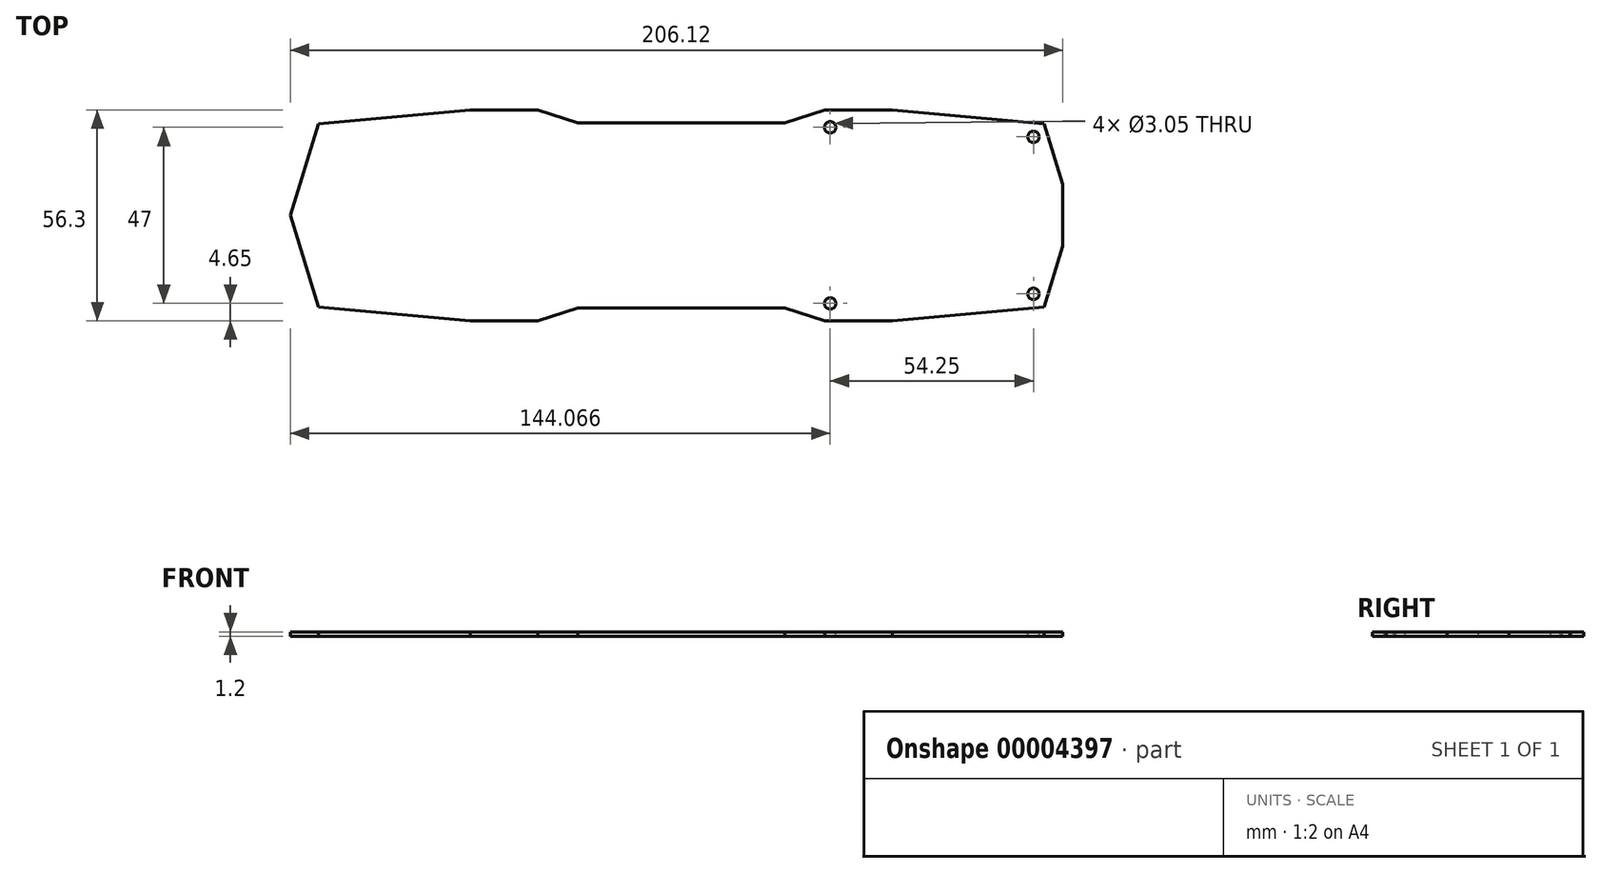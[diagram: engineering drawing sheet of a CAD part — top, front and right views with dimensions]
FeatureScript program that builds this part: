
annotation { "Feature Type Name" : "Feature", "Feature Type Description" : "" }
export const myFeature = defineFeature(function(context is Context, id is Id, definition is map)
    precondition{}
    {
        {
            var Q0;
            Q0=qCreatedBy(makeId("Top.planeOp"),FACE);
            var sketch = newSketch(context, id + "F0", { "sketchPlane" : qUnion([Q0])});
            skLineSegment(sketch, "E0", {"start": v(0, 0) * mm, "end": v(-206.12, 0) * mm, "construction": true});
            skLineSegment(sketch, "E1", {"start": v(0, 0) * mm, "end": v(0, 8.25) * mm});
            skLineSegment(sketch, "E2", {"start": v(0, 8.25) * mm, "end": v(-4.97, 24.5) * mm});
            skLineSegment(sketch, "E3", {"start": v(-4.97, 24.5) * mm, "end": v(-45.5, 28.15) * mm});
            skLineSegment(sketch, "E4.trimOffspring", {"start": v(-45.5, 28.15) * mm, "end": v(-63.5, 28.15) * mm});
            skLineSegment(sketch, "E5.0", {"start": v(-101.8, 0) * mm, "end": v(-101.8, 28.15) * mm, "construction": true});
            skPoint(sketch, "E6.orphan", {"position": v(0, -28.15) * mm});
            skPoint(sketch, "E7.orphan", {"position": v(-205, -28.15) * mm});
            skPoint(sketch, "E8.start.orphan", {"position": v(-205, 28.15) * mm});
            skLineSegment(sketch, "E9.0.MirrorCS", {"start": v(-206.12, 0) * mm, "end": v(-198.63, 24.5) * mm});
            skLineSegment(sketch, "E9.1.MirrorCS", {"start": v(-158.1, 28.15) * mm, "end": v(-140.1, 28.15) * mm});
            skLineSegment(sketch, "E9.3.MirrorCS", {"start": v(-198.63, 24.5) * mm, "end": v(-158.1, 28.15) * mm});
            skPoint(sketch, "E10.orphan", {"position": v(-205, 0) * mm});
            skLineSegment(sketch, "E11.1.MirrorCS", {"start": v(-203.6, 8.25) * mm, "end": v(-198.63, 24.5) * mm});
            skPoint(sketch, "E11.5.MirrorP", {"position": v(1.4, 28.15) * mm});
            skLineSegment(sketch, "E12.0.MirrorCS", {"start": v(-203.6, -8.25) * mm, "end": v(-198.63, -24.5) * mm});
            skLineSegment(sketch, "E12.1.MirrorCS", {"start": v(-158.1, -28.15) * mm, "end": v(-140.1, -28.15) * mm});
            skLineSegment(sketch, "E12.2.MirrorCS", {"start": v(-4.97, -24.5) * mm, "end": v(-45.5, -28.15) * mm});
            skLineSegment(sketch, "E12.3.MirrorCS", {"start": v(-198.63, -24.5) * mm, "end": v(-158.1, -28.15) * mm});
            skLineSegment(sketch, "E12.4.MirrorCS", {"start": v(-45.5, -28.15) * mm, "end": v(-63.5, -28.15) * mm});
            skLineSegment(sketch, "E12.5.MirrorCS", {"start": v(0, -8.25) * mm, "end": v(-4.97, -24.5) * mm});
            skPoint(sketch, "E12.6.MirrorP", {"position": v(1.4, -28.15) * mm});
            skLineSegment(sketch, "E12.7.MirrorCS", {"start": v(-198.63, -24.5) * mm, "end": v(-158.1, -28.15) * mm});
            skLineSegment(sketch, "E12.8.MirrorCS", {"start": v(-206.12, 0) * mm, "end": v(-198.63, -24.5) * mm});
            skLineSegment(sketch, "E12.11.MirrorCS", {"start": v(-45.5, -28.15) * mm, "end": v(-63.5, -28.15) * mm});
            skLineSegment(sketch, "E12.12.MirrorCS", {"start": v(0, 0) * mm, "end": v(0, -8.25) * mm});
            skLineSegment(sketch, "E12.13.MirrorCS", {"start": v(0, -8.25) * mm, "end": v(-4.97, -24.5) * mm});
            skLineSegment(sketch, "E12.14.MirrorCS", {"start": v(-4.97, -24.5) * mm, "end": v(-45.5, -28.15) * mm});
            skLineSegment(sketch, "E12.15.MirrorCS", {"start": v(-101.8, 0) * mm, "end": v(-101.8, -28.15) * mm, "construction": true});
            skLineSegment(sketch, "E12.16.MirrorCS", {"start": v(-158.1, -28.15) * mm, "end": v(-140.1, -28.15) * mm});
            skPoint(sketch, "E13.orphan", {"position": v(2.52, 0) * mm});
            skPoint(sketch, "E11.0.MirrorCS.start.orphan", {"position": v(-203.6, 0) * mm});
            skLineSegment(sketch, "E14", {"start": v(-74.2, 24.75) * mm, "end": v(-63.5, 28.15) * mm});
            skLineSegment(sketch, "E15", {"start": v(-74.2, -24.75) * mm, "end": v(-63.5, -28.15) * mm});
            skLineSegment(sketch, "E16.0.MirrorCS", {"start": v(-129.4, 24.75) * mm, "end": v(-140.1, 28.15) * mm});
            skLineSegment(sketch, "E17.0.MirrorCS", {"start": v(-129.4, -24.75) * mm, "end": v(-140.1, -28.15) * mm});
            skLineSegment(sketch, "E18.trimOffspring", {"start": v(-74.2, -24.75) * mm, "end": v(-129.4, -24.75) * mm});
            skLineSegment(sketch, "E19.trimOffspring", {"start": v(-74.2, 24.75) * mm, "end": v(-129.4, 24.75) * mm});
            skSolve(sketch);
        }
        {
            var Q0;
            Q0=qSketchRegion(id+"F0",true);
            extrude(context, id + "F1", {"entities" : qUnion([Q0]), "depth" : 1.2 * mm});
        }
        {
            var Q0;
            Q0=makeQuery(id+"F1.opExtrude","CAP_FACE",FACE,{"disambiguationData":[OSD([sQuery(id+"F0.wireOp",EDGE,"E11.1.MirrorCS"),sQuery(id+"F0.wireOp",EDGE,"E2"),sQuery(id+"F0.wireOp",EDGE,"E4.trimOffspring"),sQuery(id+"F0.wireOp",EDGE,"E3"),sQuery(id+"F0.wireOp",EDGE,"E9.3.MirrorCS"),sQuery(id+"F0.wireOp",EDGE,"E9.1.MirrorCS"),sQuery(id+"F0.wireOp",EDGE,"E12.7.MirrorCS"),sQuery(id+"F0.wireOp",EDGE,"E12.8.MirrorCS"),sQuery(id+"F0.wireOp",EDGE,"E12.11.MirrorCS"),sQuery(id+"F0.wireOp",EDGE,"E12.12.MirrorCS"),sQuery(id+"F0.wireOp",EDGE,"E12.13.MirrorCS"),sQuery(id+"F0.wireOp",EDGE,"E12.14.MirrorCS"),sQuery(id+"F0.wireOp",EDGE,"E12.16.MirrorCS"),sQuery(id+"F0.wireOp",EDGE,"E14"),sQuery(id+"F0.wireOp",EDGE,"E15"),sQuery(id+"F0.wireOp",EDGE,"E16.0.MirrorCS"),sQuery(id+"F0.wireOp",EDGE,"E17.0.MirrorCS"),sQuery(id+"F0.wireOp",EDGE,"E18.trimOffspring"),sQuery(id+"F0.wireOp",EDGE,"E19.trimOffspring")])],"isStart":false});
            var sketch = newSketch(context, id + "F2", { "sketchPlane" : qUnion([Q0])});
            skLineSegment(sketch, "E20.0", {"start": v(-3.59, 7.15) * mm, "end": v(-8.55, 23.4) * mm, "construction": true});
            skLineSegment(sketch, "E21.0", {"start": v(-3.59, -7.15) * mm, "end": v(-8.55, -23.4) * mm, "construction": true});
            skLineSegment(sketch, "E22", {"start": v(0, 0) * mm, "end": v(-60.09, 0) * mm, "construction": true});
            skLineSegment(sketch, "E23.0", {"start": v(0, 20.95) * mm, "end": v(-60.09, 20.95) * mm, "construction": true});
            skLineSegment(sketch, "E24.0", {"start": v(0, -20.95) * mm, "end": v(-60.09, -20.95) * mm, "construction": true});
            skCircle(sketch, "E25", {"center": v(-7.8, 20.95) * mm, "radius": 1.52 * mm});
            skCircle(sketch, "E26", {"center": v(-7.8, -20.95) * mm, "radius": 1.52 * mm});
            skSolve(sketch);
        }
        {
            var Q0;
            {Q0=qUnion([makeQuery(id+"F2.imprint","IMPRINT",FACE,{"disambiguationData":[TD([[makeQuery(id+"F2.imprint","IMPRINT",EDGE,{"derivedFrom":sQuery(id+"F2.wireOp",EDGE,"E25")}),1.0]])]}),makeQuery(id+"F2.imprint","IMPRINT",FACE,{"disambiguationData":[TD([[makeQuery(id+"F2.imprint","IMPRINT",EDGE,{"derivedFrom":sQuery(id+"F2.wireOp",EDGE,"E26")}),1.0]])]})]);}
            extrude(context, id + "F3", {"entities" : qUnion([Q0]), "operationType" : NewBodyOperationType.REMOVE, "endBound" : BoundingType.THROUGH_ALL, "oppositeDirection" : true, "depth" : 25 * mm});
        }
        {
            var Q0;
            Q0=makeQuery(id+"F1.opExtrude","CAP_FACE",FACE,{"disambiguationData":[OSD([sQuery(id+"F0.wireOp",EDGE,"E11.1.MirrorCS"),sQuery(id+"F0.wireOp",EDGE,"E2"),sQuery(id+"F0.wireOp",EDGE,"E4.trimOffspring"),sQuery(id+"F0.wireOp",EDGE,"E3"),sQuery(id+"F0.wireOp",EDGE,"E9.3.MirrorCS"),sQuery(id+"F0.wireOp",EDGE,"E9.1.MirrorCS"),sQuery(id+"F0.wireOp",EDGE,"E12.7.MirrorCS"),sQuery(id+"F0.wireOp",EDGE,"E12.8.MirrorCS"),sQuery(id+"F0.wireOp",EDGE,"E12.11.MirrorCS"),sQuery(id+"F0.wireOp",EDGE,"E12.12.MirrorCS"),sQuery(id+"F0.wireOp",EDGE,"E12.13.MirrorCS"),sQuery(id+"F0.wireOp",EDGE,"E12.14.MirrorCS"),sQuery(id+"F0.wireOp",EDGE,"E12.16.MirrorCS"),sQuery(id+"F0.wireOp",EDGE,"E14"),sQuery(id+"F0.wireOp",EDGE,"E15"),sQuery(id+"F0.wireOp",EDGE,"E16.0.MirrorCS"),sQuery(id+"F0.wireOp",EDGE,"E17.0.MirrorCS"),sQuery(id+"F0.wireOp",EDGE,"E18.trimOffspring"),sQuery(id+"F0.wireOp",EDGE,"E19.trimOffspring")])],"isStart":false});
            var sketch = newSketch(context, id + "F4", { "sketchPlane" : qUnion([Q0])});
            skLineSegment(sketch, "E27", {"start": v(-7.8, 20.95) * mm, "end": v(-7.8, -20.95) * mm, "construction": true});
            skLineSegment(sketch, "E28.0", {"start": v(-62.05, 23.5) * mm, "end": v(-62.05, -23.5) * mm, "construction": true});
            skLineSegment(sketch, "E29", {"start": v(-7.8, 0) * mm, "end": v(-62.05, 0) * mm, "construction": true});
            skLineSegment(sketch, "E30.0", {"start": v(-7.8, 23.5) * mm, "end": v(-62.05, 23.5) * mm, "construction": true});
            skLineSegment(sketch, "E31.0", {"start": v(-7.8, -23.5) * mm, "end": v(-62.05, -23.5) * mm, "construction": true});
            skPoint(sketch, "E32.orphan", {"position": v(-62.05, 20.95) * mm});
            skPoint(sketch, "E33.orphan", {"position": v(-62.05, -20.95) * mm});
            skCircle(sketch, "E34", {"center": v(-62.05, 23.5) * mm, "radius": 1.52 * mm});
            skCircle(sketch, "E35", {"center": v(-62.05, -23.5) * mm, "radius": 1.52 * mm});
            skSolve(sketch);
        }
        {
            var Q0;
            {Q0=qUnion([makeQuery(id+"F4.imprint","IMPRINT",FACE,{"disambiguationData":[TD([[makeQuery(id+"F4.imprint","IMPRINT",EDGE,{"derivedFrom":sQuery(id+"F4.wireOp",EDGE,"E34")}),1.0]])]}),makeQuery(id+"F4.imprint","IMPRINT",FACE,{"disambiguationData":[TD([[makeQuery(id+"F4.imprint","IMPRINT",EDGE,{"derivedFrom":sQuery(id+"F4.wireOp",EDGE,"E35")}),1.0]])]})]);}
            extrude(context, id + "F5", {"entities" : qUnion([Q0]), "operationType" : NewBodyOperationType.REMOVE, "endBound" : BoundingType.THROUGH_ALL, "oppositeDirection" : true, "depth" : 25 * mm});
        }
    });
